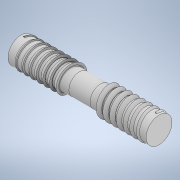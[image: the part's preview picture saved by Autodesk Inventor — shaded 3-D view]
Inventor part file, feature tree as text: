
AUTODESK INVENTOR PART (.ipt)
format: ipt  version: 2020 (Build 240168000, 168)  size: 430,080 bytes
history: native  units: mm
features: sketch x2, revolve x1, helix x1, mirror x1, projected_geometry x1
ambient origin geometry x8: Origin, YZ Plane, XZ Plane, XY Plane, X Axis, Y Axis, Z Axis, Center Point
bodies: Solid1 (feature_tree)
feature tree (6):
  revolve  "Revolution1"  [1 undecoded]
  helix  "Coil1"  [1 undecoded]
  mirror  "Mirror1"
  sketch  "Sketch1"  dims[d0=36.0mm d1=6.75mm d2=0.0mm]
  sketch  "Sketch2"  dims[d3=6.75mm d5=90.0deg d11=3.5mm d12=25.5mm d13=10.0mm d14=0.0mm d15=90.0deg d16=90.0deg d17=0.0mm d18=0.0mm d19=5.5mm d20=5.5mm d22=1.1mm d23=2.068116mm]
  projected_geometry  "Projected Loop1"
note: 2 required parameter values undecoded (feature->parameter linkage not recoverable at this tier; creation-order binding heuristic only, values carry confidence <= 0.55)